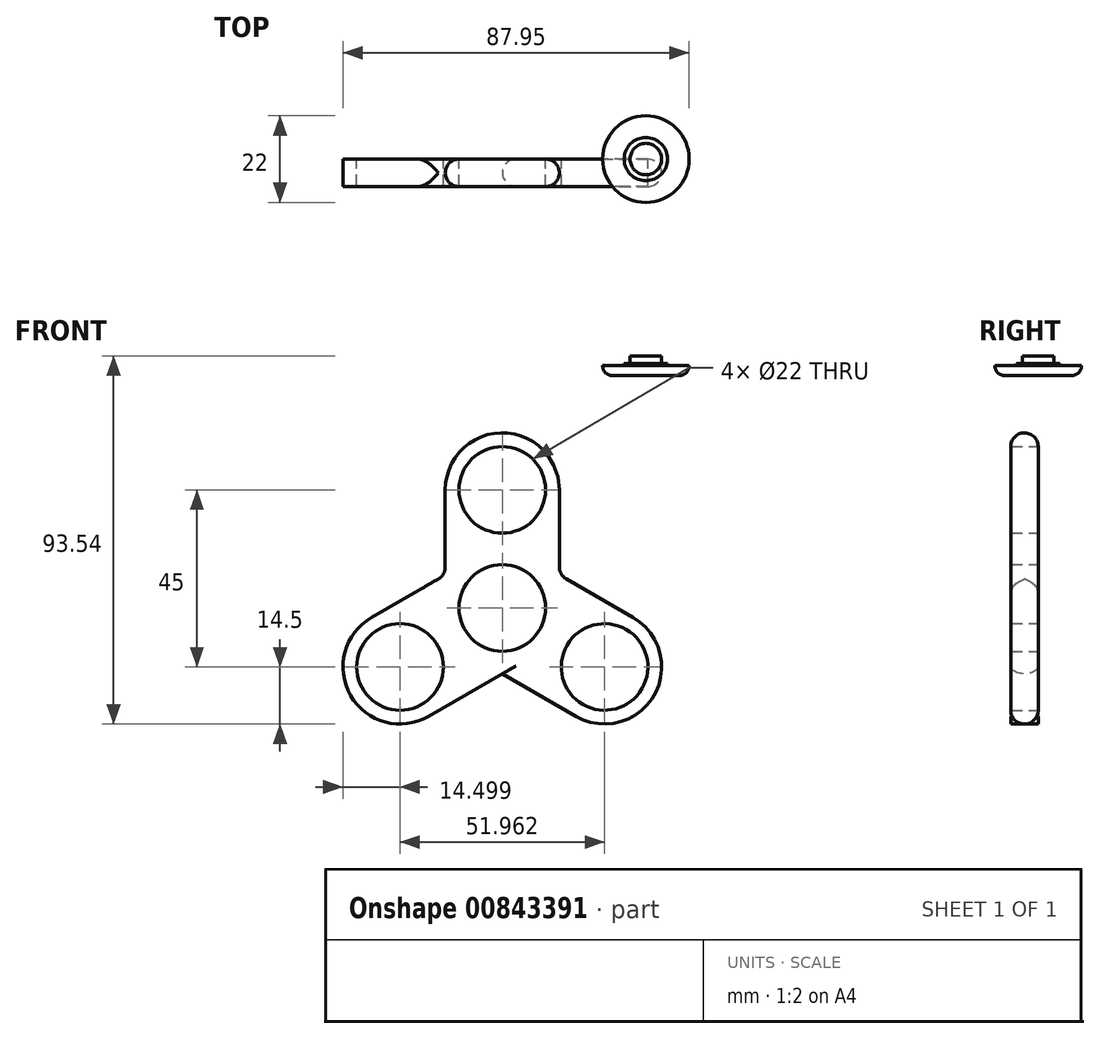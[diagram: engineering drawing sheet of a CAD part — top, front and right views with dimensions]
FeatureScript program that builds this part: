
annotation { "Feature Type Name" : "Feature", "Feature Type Description" : "" }
export const myFeature = defineFeature(function(context is Context, id is Id, definition is map)
    precondition{}
    {
        {
            var Q0;
            Q0=qCreatedBy(makeId("Front.planeOp"),FACE);
            var sketch = newSketch(context, id + "F0", { "sketchPlane" : qUnion([Q0])});
            skCircle(sketch, "E0", {"center": v(0, 0) * mm, "radius": 11 * mm});
            skCircle(sketch, "E1", {"center": v(0, 30) * mm, "radius": 11 * mm});
            skArc(sketch, "E2", {"start": v(14.5, 30) * mm, "mid": v(0, 44.5) * mm, "end": v(-14.5, 30) * mm});
            skLineSegment(sketch, "E3", {"start": v(14.5, 30) * mm, "end": v(14.5, 8.37) * mm});
            skLineSegment(sketch, "E4", {"start": v(-14.5, 30) * mm, "end": v(-14.5, 8.37) * mm});
            skLineSegment(sketch, "E5.1.0", {"start": v(-18.73, -27.56) * mm, "end": v(0, -16.74) * mm});
            skArc(sketch, "E5.1.1", {"start": v(-33.23, -2.44) * mm, "mid": v(-38.54, -22.25) * mm, "end": v(-18.73, -27.56) * mm});
            skCircle(sketch, "E5.1.2", {"center": v(-25.98, -15) * mm, "radius": 11 * mm});
            skLineSegment(sketch, "E5.1.3", {"start": v(-33.23, -2.44) * mm, "end": v(-14.5, 8.37) * mm});
            skLineSegment(sketch, "E5.2.0", {"start": v(33.23, -2.44) * mm, "end": v(14.5, 8.37) * mm});
            skArc(sketch, "E5.2.1", {"start": v(18.73, -27.56) * mm, "mid": v(38.54, -22.25) * mm, "end": v(33.23, -2.44) * mm});
            skCircle(sketch, "E5.2.2", {"center": v(25.98, -15) * mm, "radius": 11 * mm});
            skLineSegment(sketch, "E5.2.3", {"start": v(18.73, -27.56) * mm, "end": v(0, -16.74) * mm});
            skPoint(sketch, "E6.orphan", {"position": v(-14.5, 0) * mm});
            skPoint(sketch, "E7.orphan", {"position": v(-7.25, 12.56) * mm});
            skPoint(sketch, "E8.orphan", {"position": v(7.25, 12.56) * mm});
            skPoint(sketch, "E9.orphan", {"position": v(14.5, 0) * mm});
            skPoint(sketch, "E10.orphan", {"position": v(7.25, -12.56) * mm});
            skPoint(sketch, "E11.orphan", {"position": v(-7.25, -12.56) * mm});
            skSolve(sketch);
        }
        {
            var Q0;
            Q0=makeQuery(id+"F0.imprint","IMPRINT",FACE,{"disambiguationData":[TD([[makeQuery(id+"F0.imprint","IMPRINT",EDGE,{"derivedFrom":sQuery(id+"F0.wireOp",EDGE,"E0")}),-1.0]])]});
            extrude(context, id + "F1", {"entities" : qUnion([Q0]), "depth" : 7 * mm, "offsetDistance" : 25 * mm});
        }
        {
            var Q0;
            Q0=makeQuery(id+"F1.opExtrude","SWEPT_FACE",FACE,{"disambiguationData":[OSD([sQuery(id+"F0.wireOp",EDGE,"E4")])]});
            var Q1;
            Q1=makeQuery(id+"F1.opExtrude","SWEPT_FACE",FACE,{"disambiguationData":[OSD([sQuery(id+"F0.wireOp",EDGE,"E5.2.0")])]});
            fillet(context, id + "F2", {"entities" : qUnion([Q0, Q1]), "radius" : 3.5 * mm, "tangentPropagation" : true, "allowEdgeOverflow" : false});
        }
        {
            var Q0;
            Q0=qCreatedBy(makeId("Front.planeOp"),FACE);
            var sketch = newSketch(context, id + "F3", { "sketchPlane" : qUnion([Q0])});
            skLineSegment(sketch, "E12", {"start": v(36.47, 59.04) * mm, "end": v(47.47, 59.04) * mm});
            skLineSegment(sketch, "E13", {"start": v(47.47, 59.04) * mm, "end": v(47.47, 61.54) * mm});
            skLineSegment(sketch, "E14", {"start": v(47.47, 61.54) * mm, "end": v(41.97, 61.54) * mm});
            skLineSegment(sketch, "E15", {"start": v(41.97, 61.54) * mm, "end": v(41.97, 62.04) * mm});
            skLineSegment(sketch, "E16", {"start": v(41.97, 62.04) * mm, "end": v(40.47, 62.04) * mm});
            skLineSegment(sketch, "E17", {"start": v(40.47, 62.04) * mm, "end": v(40.47, 64.04) * mm});
            skLineSegment(sketch, "E18", {"start": v(40.47, 64.04) * mm, "end": v(36.47, 64.04) * mm});
            skLineSegment(sketch, "E19", {"start": v(36.47, 64.04) * mm, "end": v(36.47, 59.04) * mm});
            skSolve(sketch);
        }
        {
            var Q0;
            Q0=makeQuery(id+"F3.imprint","IMPRINT",FACE,{"disambiguationData":[TD([[makeQuery(id+"F3.imprint","IMPRINT",EDGE,{"derivedFrom":sQuery(id+"F3.wireOp",EDGE,"E12")}),1.0]])]});
            var Q1;
            Q1=sQuery(id+"F3.wireOp",EDGE,"E19");
            revolve(context, id + "F4", {"surfaceOperationType" : NewSurfaceOperationType.NEW, "entities" : qUnion([Q0]), "axis" : qUnion([Q1]), "revolveType" : RevolveType.FULL});
        }
        {
            var Q0;
            Q0=makeQuery(id+"F4.opRevolve","SWEPT_FACE",FACE,{"disambiguationData":[OSD([sQuery(id+"F3.wireOp",EDGE,"E12")])]});
            fillet(context, id + "F5", {"entities" : qUnion([Q0]), "radius" : 2.5 * mm, "tangentPropagation" : true, "allowEdgeOverflow" : false});
        }
    });
